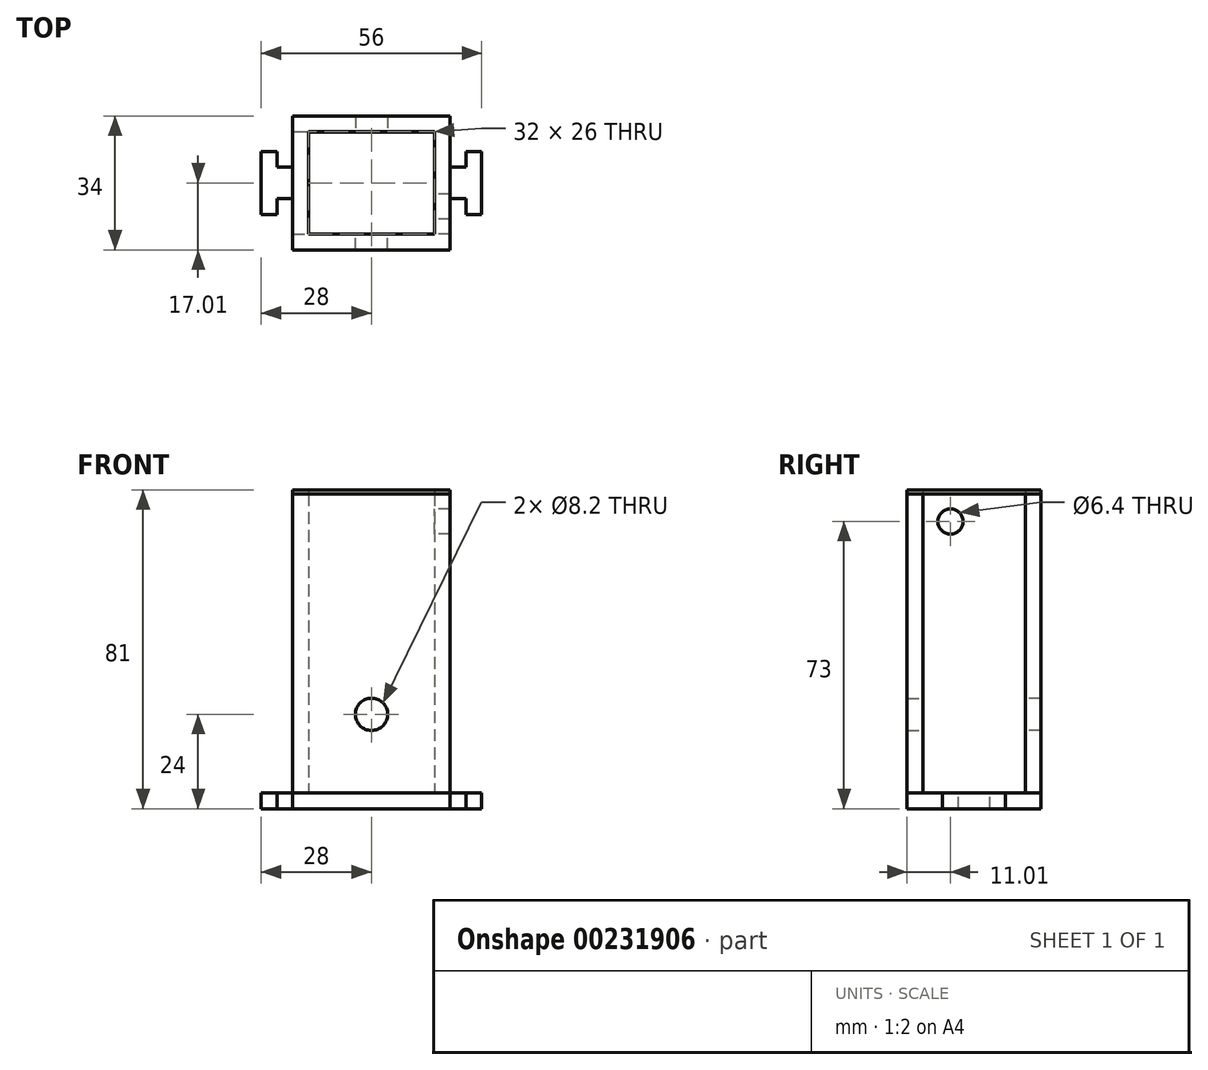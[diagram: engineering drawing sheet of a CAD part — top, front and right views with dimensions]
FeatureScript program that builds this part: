
annotation { "Feature Type Name" : "Feature", "Feature Type Description" : "" }
export const myFeature = defineFeature(function(context is Context, id is Id, definition is map)
    precondition{}
    {
        {
            var Q0;
            Q0=qCreatedBy(makeId("Front.planeOp"),FACE);
            var sketch = newSketch(context, id + "F0", { "sketchPlane" : qUnion([Q0])});
            skLineSegment(sketch, "E0.bottom", {"start": v(20, -20) * mm, "end": v(-20, -20) * mm});
            skLineSegment(sketch, "E0.top", {"start": v(20, 56) * mm, "end": v(-20, 56) * mm});
            skLineSegment(sketch, "E0.left", {"start": v(20, -20) * mm, "end": v(20, 56) * mm});
            skLineSegment(sketch, "E0.right", {"start": v(-20, -20) * mm, "end": v(-20, 56) * mm});
            skPoint(sketch, "E0.middle", {"position": v(0, 18) * mm});
            skCircle(sketch, "E1", {"center": v(0, 0) * mm, "radius": 4.1 * mm});
            skSolve(sketch);
        }
        {
            var Q0;
            Q0 = qSketchRegion(id + "F0", true);
            extrude(context, id + "F1", {"entities" : qUnion([Q0]), "depth" : 4 * mm});
        }
        {
            var Q0;
            Q0=qCreatedBy(makeId("Right.planeOp"),FACE);
            var sketch = newSketch(context, id + "F2", { "sketchPlane" : qUnion([Q0])});
            skLineSegment(sketch, "E2.bottom", {"start": v(0, 56) * mm, "end": v(26, 56) * mm});
            skLineSegment(sketch, "E2.top", {"start": v(0, -20) * mm, "end": v(26.01, -20) * mm});
            skLineSegment(sketch, "E2.left", {"start": v(0, 56) * mm, "end": v(0.01, -20) * mm});
            skLineSegment(sketch, "E2.right", {"start": v(26, 56) * mm, "end": v(26.01, -20) * mm});
            skCircle(sketch, "E3", {"center": v(7, 49) * mm, "radius": 3.2 * mm});
            skSolve(sketch);
        }
        {
            var Q0;
            Q0=makeQuery(id+"F2.imprint","IMPRINT",FACE,{"disambiguationData":[TD([[makeQuery(id+"F2.imprint","IMPRINT",EDGE,{"derivedFrom":sQuery(id+"F2.wireOp",EDGE,"E2.bottom")}),-1.0]])]});
            extrude(context, id + "F3", {"entities" : qUnion([Q0]), "operationType" : NewBodyOperationType.ADD, "depth" : 20 * mm, "hasSecondDirection" : true, "secondDirectionOppositeDirection" : false, "secondDirectionDepth" : 16 * mm});
        }
        {
            var Q0;
            Q0=makeQuery(id+"F2.imprint","IMPRINT",FACE,{"disambiguationData":[TD([[makeQuery(id+"F2.imprint","IMPRINT",EDGE,{"derivedFrom":sQuery(id+"F2.wireOp",EDGE,"E3")}),1.0]])]});
            var Q1;
            Q1=makeQuery(id+"F2.imprint","IMPRINT",FACE,{"disambiguationData":[TD([[makeQuery(id+"F2.imprint","IMPRINT",EDGE,{"derivedFrom":sQuery(id+"F2.wireOp",EDGE,"E2.bottom")}),-1.0]])]});
            extrude(context, id + "F4", {"entities" : qUnion([Q0, Q1]), "oppositeDirection" : true, "depth" : 20 * mm, "hasSecondDirection" : true, "secondDirectionOppositeDirection" : true, "secondDirectionDepth" : 16 * mm});
        }
        {
            var Q0;
            Q0=makeQuery(id+"F0.imprint","IMPRINT",FACE,{"disambiguationData":[TD([[makeQuery(id+"F0.imprint","IMPRINT",EDGE,{"derivedFrom":sQuery(id+"F0.wireOp",EDGE,"E0.bottom")}),-1.0]])]});
            extrude(context, id + "F5", {"entities" : qUnion([Q0]), "oppositeDirection" : true, "depth" : 30 * mm, "hasSecondDirection" : true, "secondDirectionOppositeDirection" : true, "secondDirectionDepth" : 26 * mm});
        }
        {
            var Q0;
            Q0=qCreatedBy(makeId("Top.planeOp"),FACE);
            var sketch = newSketch(context, id + "F6", { "sketchPlane" : qUnion([Q0])});
            skLineSegment(sketch, "E4.bottom", {"start": v(-20, -4) * mm, "end": v(20, -4) * mm});
            skLineSegment(sketch, "E4.top", {"start": v(-20, 30) * mm, "end": v(20, 30) * mm});
            skLineSegment(sketch, "E4.left", {"start": v(-20, -4) * mm, "end": v(-20, 30) * mm});
            skLineSegment(sketch, "E4.right", {"start": v(20, -4) * mm, "end": v(20, 30) * mm});
            skLineSegment(sketch, "E5.bottom", {"start": v(20, 17) * mm, "end": v(24, 17) * mm});
            skLineSegment(sketch, "E5.top", {"start": v(20, 9) * mm, "end": v(24, 9) * mm});
            skLineSegment(sketch, "E5.left", {"start": v(20, 17) * mm, "end": v(20, 9) * mm});
            skLineSegment(sketch, "E5.right", {"start": v(24, 17) * mm, "end": v(24, 9) * mm});
            skPoint(sketch, "E5.middle", {"position": v(22, 13) * mm});
            skPoint(sketch, "E5.middle.positionSnap0", {"position": v(20, 13) * mm});
            skPoint(sketch, "E5.centerSnap0", {"position": v(20, 13) * mm});
            skLineSegment(sketch, "E6.bottom", {"start": v(-20, 17) * mm, "end": v(-24, 17) * mm});
            skLineSegment(sketch, "E6.top", {"start": v(-20, 9) * mm, "end": v(-24, 9) * mm});
            skLineSegment(sketch, "E6.left", {"start": v(-20, 17) * mm, "end": v(-20, 9) * mm});
            skLineSegment(sketch, "E6.right", {"start": v(-24, 17) * mm, "end": v(-24, 9) * mm});
            skPoint(sketch, "E6.middle", {"position": v(-22, 13) * mm});
            skPoint(sketch, "E6.middle.positionSnap0", {"position": v(-20, 13) * mm});
            skPoint(sketch, "E6.cornerSnap0", {"position": v(-20, 13) * mm});
            skPoint(sketch, "E6.centerSnap0", {"position": v(-20, 13) * mm});
            skLineSegment(sketch, "E7.bottom", {"start": v(24, 21) * mm, "end": v(28, 21) * mm});
            skLineSegment(sketch, "E7.top", {"start": v(24, 5) * mm, "end": v(28, 5) * mm});
            skLineSegment(sketch, "E7.left", {"start": v(24, 21) * mm, "end": v(24, 5) * mm});
            skLineSegment(sketch, "E7.right", {"start": v(28, 21) * mm, "end": v(28, 5) * mm});
            skPoint(sketch, "E7.middle", {"position": v(26, 13) * mm});
            skPoint(sketch, "E7.cornerSnap0", {"position": v(24, 13) * mm});
            skLineSegment(sketch, "E8.bottom", {"start": v(-24, 21) * mm, "end": v(-28, 21) * mm});
            skLineSegment(sketch, "E8.top", {"start": v(-24, 5) * mm, "end": v(-28, 5) * mm});
            skLineSegment(sketch, "E8.left", {"start": v(-24, 21) * mm, "end": v(-24, 5) * mm});
            skLineSegment(sketch, "E8.right", {"start": v(-28, 21) * mm, "end": v(-28, 5) * mm});
            skPoint(sketch, "E8.middle", {"position": v(-26, 13) * mm});
            skPoint(sketch, "E8.cornerSnap0", {"position": v(-24, 13) * mm});
            skSolve(sketch);
        }
        {
            var Q0;
            Q0 = qSketchRegion(id + "F6", true);
            extrude(context, id + "F7", {"entities" : qUnion([Q0]), "oppositeDirection" : true, "depth" : 24 * mm, "hasSecondDirection" : true, "secondDirectionOppositeDirection" : true, "secondDirectionDepth" : 20 * mm});
        }
        {
            var Q0;
            Q0=qCreatedBy(makeId("Top.planeOp"),FACE);
            var sketch = newSketch(context, id + "F8", { "sketchPlane" : qUnion([Q0])});
            skLineSegment(sketch, "E9.bottom", {"start": v(-20, -4) * mm, "end": v(20, -4) * mm});
            skLineSegment(sketch, "E9.top", {"start": v(-20, 30) * mm, "end": v(20, 30) * mm});
            skLineSegment(sketch, "E9.left", {"start": v(-20, -4) * mm, "end": v(-20, 30) * mm});
            skLineSegment(sketch, "E9.right", {"start": v(20, -4) * mm, "end": v(20, 30) * mm});
            skLineSegment(sketch, "E10.bottom", {"start": v(-16, 0) * mm, "end": v(16, 0) * mm});
            skLineSegment(sketch, "E10.top", {"start": v(-16, 26) * mm, "end": v(16, 26) * mm});
            skLineSegment(sketch, "E10.left", {"start": v(-16, 0) * mm, "end": v(-16, 26) * mm});
            skLineSegment(sketch, "E10.right", {"start": v(16, 0) * mm, "end": v(16, 26) * mm});
            skSolve(sketch);
        }
        {
            var Q0;
            Q0 = qSketchRegion(id + "F8", true);
            var Q1;
            Q1=makeQuery(id+"F4.opExtrude","SWEPT_FACE",FACE,{"disambiguationData":[OSD([sQuery(id+"F2.wireOp",EDGE,"E2.bottom")])]});
            extrude(context, id + "F9", {"entities" : qUnion([Q0]), "endBoundEntityFace" : qUnion([Q1]), "depth" : 57 * mm, "hasSecondDirection" : true, "secondDirectionOppositeDirection" : false, "secondDirectionDepth" : 56 * mm});
        }
    });
